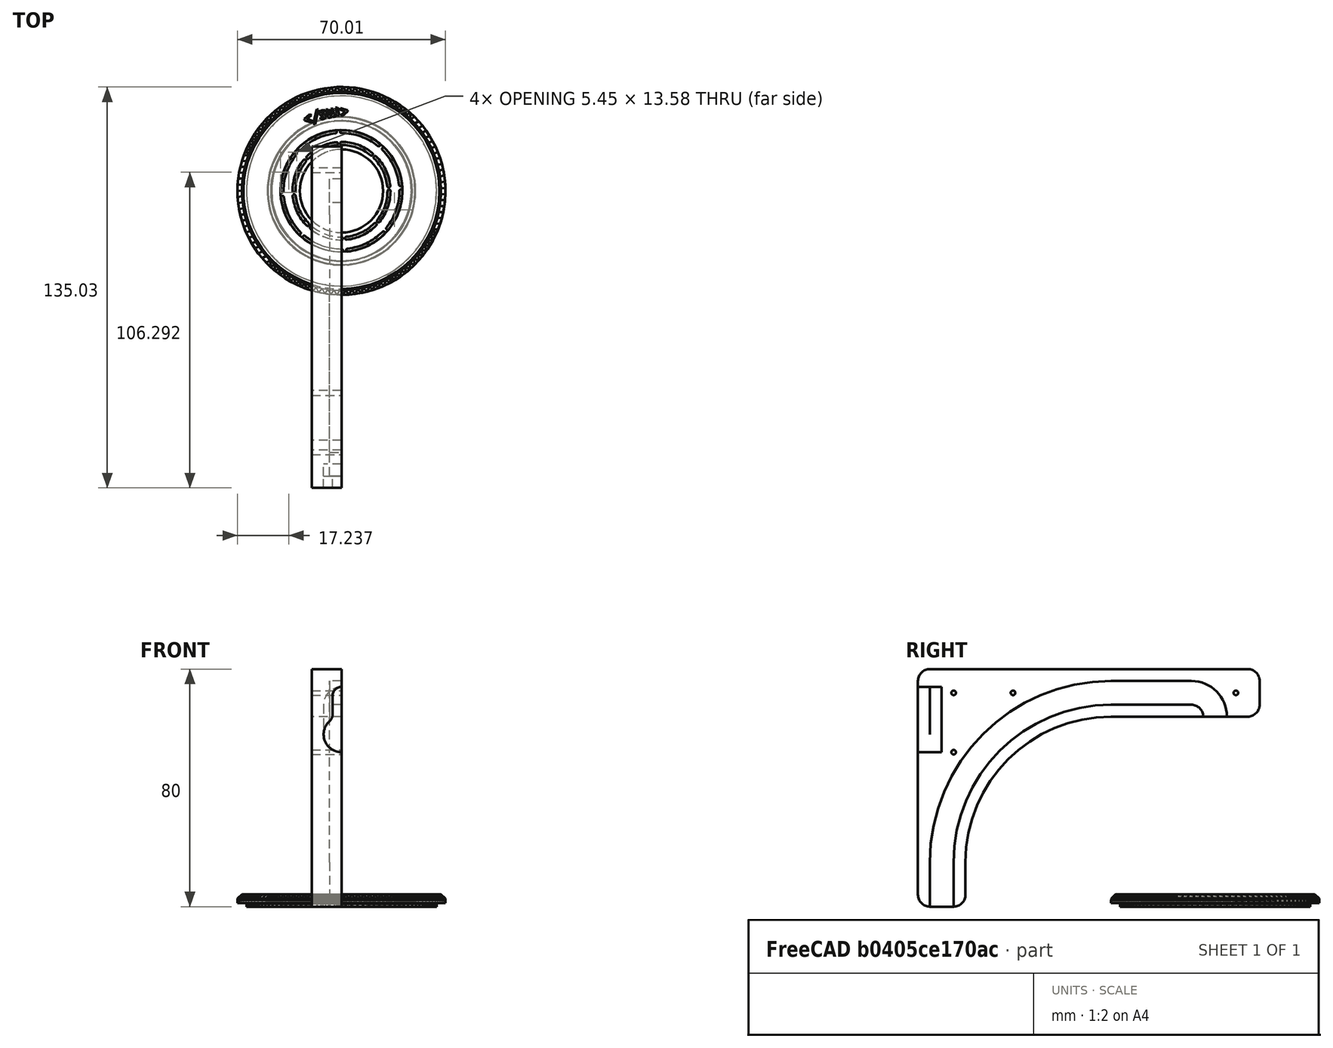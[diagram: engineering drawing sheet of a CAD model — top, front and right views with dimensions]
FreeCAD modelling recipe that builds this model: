
FCSTD DOCUMENT  (FreeCAD 1.0R39109 (Git))
Label: lampshade
License: All rights reserved
LicenseURL: http://www.ohwr.org/attachments/2388/cern_ohl_v_1_2.txt
objects: Sketcher::SketchObject×11, PartDesign::Pocket×6, PartDesign::Pad×5, Part::Feature×4, Mesh::Feature×3, PartDesign::SubShapeBinder×3, PartDesign::Body×3, PartDesign::PolarPattern×2, PartDesign::Chamfer×1, PartDesign::Fillet×1, Part::FeaturePython×1, Part::Mirroring×1
note: 77 computed .brp shape members not serialized (recipe doc carries the construction recipe); baked Part::Feature solids carry a one-line shape summary decoded from their .brp

FEATURE [Mesh::Feature] obj_1_Checkerboard_v6  label="obj_1_Checkerboard v6"
  Placement = pos=(89.8,-89.8,1.1) rot=(0,1,0;3.14159rad)
FEATURE [Mesh::Feature] obj_2_cordset_holder_bottom__E27_  label="obj_2_cordset holder bottom (E27)"
FEATURE [Mesh::Feature] obj_1_cordset_holder_top__E27_  label="obj_1_cordset holder top (E27)"
  Placement = pos=(-68.3,-1.4,0) rot=(0,0,1;0rad)
FEATURE [Part::Feature] obj_1_cordset_holder_top__E27_001
  shape: bbox 69.98 x 69.99 x 3 mm, 2374 faces, 0 solids (baked)
FEATURE [Part::Feature] obj_1_cordset_holder_top__E27_001_solid  label="obj_1_cordset_holder_top__E27_001 (Solid)"
  Placement = pos=(-75.6225,-88.5627,1.2) rot=(0,0,1;0rad)
  shape: bbox 69.98 x 69.99 x 3 mm, 2374 faces (baked)
FEATURE [Part::Feature] obj_2_cordset_holder_bottom__E27_001
  shape: bbox 63.99 x 63.99 x 2.5 mm, 1452 faces, 0 solids (baked)
FEATURE [Part::Feature] obj_2_cordset_holder_bottom__E27_001_solid  label="obj_2_cordset_holder_bottom__E27_001 (Solid)"
  Placement = pos=(-74.9737,-87.9749,0) rot=(0,0,1;0rad)
  shape: bbox 63.99 x 63.99 x 2.5 mm, 1452 faces (baked)
FEATURE [Sketcher::SketchObject] Sketch
  ArcFitTolerance = 1e-06
  AttachmentSupport = -> [XY_Plane]
  FullyConstrained = true
  MakeInternals = false
  MapMode = 5
  sketch-geometry (2):
    g0: Circle CenterX=0 CenterY=0 CenterZ=0 NormalX=0 NormalY=0 NormalZ=1 AngleXU=0 Radius=32
    g1: Circle CenterX=0 CenterY=0 CenterZ=0 NormalX=0 NormalY=0 NormalZ=1 AngleXU=0 Radius=14
  constraints (4):
    c: Coincident(g0,g-1)
    c: Coincident(g1,g0)
    c: Diameter(g1) = 28  'dia_inner'
    c: Diameter(g0) = 64  'dia_outer'
FEATURE [PartDesign::SubShapeBinder] Binder
  BindCopyOnChange = 0
  BindMode = 0
  ClaimChildren = false
  Context = -> Body [Binder.]
  Fuse = false
  MakeFace = true
  OffsetFill = false
  OffsetIntersection = false
  OffsetJoinType = 0
  OffsetOpenResult = false
  PartialLoad = false
  Refine = true
  Relative = true
  Support = -> [obj_2_cordset_holder_bottom__E27_001_solid]
  _Version = 2
FEATURE [PartDesign::Pad] Pad
  Direction = (0,0,1)
  Length = 1
  Length2 = 10
  Profile = -> Sketch
  ReferenceAxis = -> Sketch [N_Axis]
  Refine = true
  Suppressed = false
  Type = 0
FEATURE [Sketcher::SketchObject] Sketch001
  ArcFitTolerance = 1e-06
  AttachmentSupport = -> [Pad]
  FullyConstrained = true
  MakeInternals = false
  MapMode = 5
  Placement = pos=(0,0,1) rot=(0,0,1;0rad)
  sketch-geometry (2):
    g0: Circle CenterX=0 CenterY=0 CenterZ=0 NormalX=0 NormalY=0 NormalZ=1 AngleXU=0 Radius=23.75
    g1: Circle CenterX=0 CenterY=0 CenterZ=0 NormalX=0 NormalY=0 NormalZ=1 AngleXU=0 Radius=24.75
  constraints (4):
    c: Coincident(g0,g-1)
    c: Coincident(g1,g0)
    c: Diameter(g0) = 47.5  'lip_dia_inner'
    c: Diameter(g1) = 49.5  'lip_dia_outer'
FEATURE [PartDesign::Pad] Pad001
  BaseFeature = -> Pad
  Direction = (0,0,1)
  Length = 1.5
  Length2 = 10
  Profile = -> Sketch001
  ReferenceAxis = -> Sketch001 [N_Axis]
  Refine = true
  Suppressed = false
  Type = 0
FEATURE [Sketcher::SketchObject] Sketch002
  ArcFitTolerance = 1e-06
  AttachmentSupport = -> [Pad001]
  FullyConstrained = true
  MakeInternals = false
  MapMode = 5
  Placement = pos=(0,0,1) rot=(0,0,1;0rad)
  sketch-geometry (12):
    g0: ArcOfCircle CenterX=0 CenterY=0 CenterZ=0 NormalX=0 NormalY=0 NormalZ=1 AngleXU=0 Radius=15.5 StartAngle=0.890118 EndAngle=1.5708
    g1: ArcOfCircle CenterX=0 CenterY=0 CenterZ=0 NormalX=0 NormalY=0 NormalZ=1 AngleXU=0 Radius=16.5 StartAngle=0.890118 EndAngle=1.5708
    g2: ArcOfCircle CenterX=0 CenterY=0 CenterZ=0 NormalX=0 NormalY=0 NormalZ=1 AngleXU=0 Radius=19.5 StartAngle=0.890118 EndAngle=1.5708
    g3: ArcOfCircle CenterX=0 CenterY=0 CenterZ=0 NormalX=0 NormalY=0 NormalZ=1 AngleXU=0 Radius=20.5 StartAngle=0.890118 EndAngle=1.5708
    g4: ArcOfCircle CenterX=0 CenterY=16 CenterZ=0 NormalX=0 NormalY=0 NormalZ=1 AngleXU=0 Radius=0.5 StartAngle=1.5708 EndAngle=4.71239
    g5: ArcOfCircle CenterX=0 CenterY=20 CenterZ=0 NormalX=0 NormalY=0 NormalZ=1 AngleXU=0 Radius=0.5 StartAngle=1.5708 EndAngle=4.71239
    g6: ArcOfCircle CenterX=10.0691 CenterY=12.4343 CenterZ=0 NormalX=0 NormalY=0 NormalZ=1 AngleXU=0 Radius=0.5 StartAngle=4.03171 EndAngle=7.1733
    g7: ArcOfCircle CenterX=12.5864 CenterY=15.5429 CenterZ=0 NormalX=0 NormalY=0 NormalZ=1 AngleXU=0 Radius=0.5 StartAngle=4.03171 EndAngle=7.1733
    g8: LineSegment [constr] StartX=0 StartY=20 StartZ=0 EndX=0 EndY=16 EndZ=0
    g9: LineSegment [constr] StartX=12.2717 StartY=15.1543 StartZ=0 EndX=10.0691 EndY=12.4343 EndZ=0
    g10: LineSegment [constr] StartX=9.75447 StartY=12.0458 StartZ=0 EndX=0 EndY=0 EndZ=0
    g11: LineSegment [constr] StartX=0 StartY=16 StartZ=0 EndX=0 EndY=0 EndZ=0
  constraints (32):
    c: PointOnObject(g0,g-2)
    c: PointOnObject(g11,g-2)
    c: PointOnObject(g1,g-2)
    c: PointOnObject(g2,g-2)
    c: PointOnObject(g3,g-2)
    c: Coincident(g4,g1)
    c: Coincident(g4,g0)
    c: PointOnObject(g5,g-2)
    c: Coincident(g5,g3)
    c: Coincident(g5,g2)
    c: Tangent(g6,g0) = 1.5708
    c: Tangent(g6,g1) = -1.5708
    c: Tangent(g7,g2) = 1.5708
    c: Tangent(g7,g3) = -1.5708
    c: Equal(g5,g4)
    c: Radius(g4) = 0.5
    c: DistanceY(g0,g5) = 20
    c: Coincident(g8,g5)
    c: Coincident(g8,g4)
    c: Coincident(g9,g2)
    c: Coincident(g9,g6)
    c: Coincident(g10,g0)
    c: Parallel(g10,g9)
    c: Angle(g10,g11) = 0.680678
    c: DistanceY(g-1,g4) = 16
    c: Coincident(g0,g1)
    c: Coincident(g0,g2)
    c: Coincident(g0,g3)
    c: Coincident(g0,g10)
    c: Coincident(g0,g11)
    c: Coincident(g0,g-1)
    c: Coincident(g11,g4)
FEATURE [PartDesign::Pocket] Pocket
  BaseFeature = -> Pad001
  Direction = (0,0,-1)
  Length = 5
  Length2 = 5
  Profile = -> Sketch002
  ReferenceAxis = -> Sketch002 [N_Axis]
  Refine = true
  Suppressed = false
  Type = 1
FEATURE [PartDesign::PolarPattern] PolarPattern
  Angle = 360
  Axis = -> Sketch002 [N_Axis]
  BaseFeature = -> Pocket
  Mode = 0
  Occurrences = 8
  Offset = 120
  Originals = -> [Pocket]
  Refine = true
  Suppressed = false
  TransformMode = 0
FEATURE [PartDesign::Body] Body  label="Ring_upper"
  AllowCompound = false
  Group = -> [Sketch,Binder,Pad,Sketch001,Pad001,Sketch002,Pocket,PolarPattern]
  Origin = -> Origin
  Tip = -> PolarPattern
FEATURE [PartDesign::SubShapeBinder] Binder001
  BindCopyOnChange = 0
  BindMode = 0
  ClaimChildren = false
  Context = -> Body001 [Binder001.]
  Fuse = false
  MakeFace = true
  OffsetFill = false
  OffsetIntersection = false
  OffsetJoinType = 0
  OffsetOpenResult = false
  PartialLoad = false
  Refine = true
  Relative = true
  Support = -> [obj_1_cordset_holder_top__E27_001_solid]
  _Version = 2
FEATURE [Sketcher::SketchObject] Sketch003
  ArcFitTolerance = 1e-06
  AttachmentSupport = -> [XY_Plane001]
  FullyConstrained = true
  MakeInternals = false
  MapMode = 5
  expr: Constraints[2] = Sketch.Constraints.dia_inner
  expr: Constraints[3] = Sketch.Constraints.dia_outer + 6 mm
  sketch-geometry (2):
    g0: Circle CenterX=0 CenterY=0 CenterZ=0 NormalX=0 NormalY=0 NormalZ=1 AngleXU=0 Radius=14
    g1: Circle CenterX=0 CenterY=0 CenterZ=0 NormalX=0 NormalY=0 NormalZ=1 AngleXU=0 Radius=35
  constraints (4):
    c: Coincident(g0,g-1)
    c: Coincident(g1,g0)
    c: Diameter(g0) = 28
    c: Diameter(g1) = 70
FEATURE [PartDesign::Pad] Pad002
  Direction = (0,0,1)
  Length = 3
  Length2 = 10
  Profile = -> Sketch003
  ReferenceAxis = -> Sketch003 [N_Axis]
  Refine = true
  Suppressed = false
  Type = 0
FEATURE [Sketcher::SketchObject] Sketch004
  ArcFitTolerance = 1e-06
  AttachmentSupport = -> [Pad002]
  FullyConstrained = true
  MakeInternals = false
  MapMode = 5
  Placement = pos=(0,0,0) rot=(1,0,0;3.14159rad)
  expr: Constraints[2] = Sketch001.Constraints.lip_dia_inner - 0.5 mm
  expr: Constraints[3] = Sketch001.Constraints.lip_dia_outer + 0.5 mm
  sketch-geometry (2):
    g0: Circle CenterX=0 CenterY=0 CenterZ=0 NormalX=0 NormalY=0 NormalZ=1 AngleXU=0 Radius=23.5
    g1: Circle CenterX=0 CenterY=0 CenterZ=0 NormalX=0 NormalY=0 NormalZ=1 AngleXU=0 Radius=25
  constraints (4):
    c: Coincident(g0,g-1)
    c: Coincident(g1,g0)
    c: Diameter(g0) = 47
    c: Diameter(g1) = 50
FEATURE [PartDesign::Pocket] Pocket001
  BaseFeature = -> Pad002
  Direction = (0,0,1)
  Length = 1.7
  Length2 = 5
  Profile = -> Sketch004
  ReferenceAxis = -> Sketch004 [N_Axis]
  Refine = true
  Suppressed = false
  Type = 0
FEATURE [PartDesign::SubShapeBinder] Binder002
  BindCopyOnChange = 0
  BindMode = 0
  ClaimChildren = false
  Context = -> Body001 [Binder002.]
  Fuse = false
  MakeFace = true
  OffsetFill = false
  OffsetIntersection = false
  OffsetJoinType = 0
  OffsetOpenResult = false
  PartialLoad = false
  Refine = true
  Relative = true
  Support = -> [Body]
  _Version = 2
FEATURE [Sketcher::SketchObject] Sketch005
  ArcFitTolerance = 1e-06
  AttachmentSupport = -> [Pocket001]
  ExternalGeometry = -> [Binder002]
  FullyConstrained = true
  MakeInternals = false
  MapMode = 5
  Placement = pos=(0,0,0) rot=(1,0,0;3.14159rad)
  sketch-geometry (8):
    g0: ArcOfCircle CenterX=1.4e-15 CenterY=1e-16 CenterZ=0 NormalX=0 NormalY=0 NormalZ=1 AngleXU=0 Radius=15.5 StartAngle=0.785398 EndAngle=1.46608
    g1: ArcOfCircle CenterX=1.2e-15 CenterY=8e-16 CenterZ=0 NormalX=0 NormalY=0 NormalZ=1 AngleXU=0 Radius=16.5 StartAngle=0.785398 EndAngle=1.46608
    g2: ArcOfCircle CenterX=-2.6e-15 CenterY=4e-15 CenterZ=0 NormalX=0 NormalY=0 NormalZ=1 AngleXU=0 Radius=19.5 StartAngle=0.785398 EndAngle=1.46608
    g3: ArcOfCircle CenterX=-2.5e-15 CenterY=4.2e-15 CenterZ=0 NormalX=0 NormalY=0 NormalZ=1 AngleXU=0 Radius=20.5 StartAngle=0.785398 EndAngle=1.46608
    g4: ArcOfCircle CenterX=2.09057 CenterY=19.8904 CenterZ=0 NormalX=0 NormalY=0 NormalZ=1 AngleXU=0 Radius=0.5 StartAngle=1.46608 EndAngle=4.60767
    g5: ArcOfCircle CenterX=14.1421 CenterY=14.1421 CenterZ=0 NormalX=0 NormalY=0 NormalZ=1 AngleXU=0 Radius=0.5 StartAngle=3.92699 EndAngle=7.06858
    g6: ArcOfCircle CenterX=11.3137 CenterY=11.3137 CenterZ=0 NormalX=0 NormalY=0 NormalZ=1 AngleXU=0 Radius=0.5 StartAngle=3.92699 EndAngle=7.06858
    g7: ArcOfCircle CenterX=1.67246 CenterY=15.9124 CenterZ=0 NormalX=0 NormalY=0 NormalZ=1 AngleXU=0 Radius=0.5 StartAngle=1.46608 EndAngle=4.60767
  constraints (20):
    c: Coincident(g0,g-6)
    c: Coincident(g0,g-6)
    c: Equal(g-6,g0)
    c: Coincident(g1,g-5)
    c: Coincident(g1,g-5)
    c: Equal(g1,g-5)
    c: Coincident(g2,g-4)
    c: Coincident(g2,g-4)
    c: Equal(g2,g-4)
    c: Coincident(g3,g-3)
    c: Coincident(g3,g-3)
    c: Equal(g3,g-3)
    c: Coincident(g4,g2)
    c: Tangent(g4,g3) = -1.5708
    c: Coincident(g5,g2)
    c: Tangent(g5,g3) = -1.5708
    c: Coincident(g6,g0)
    c: Tangent(g6,g1) = -1.5708
    c: Coincident(g7,g0)
    c: Tangent(g7,g1) = -1.5708
FEATURE [PartDesign::Pocket] Pocket002
  BaseFeature = -> Pocket001
  Direction = (0,0,1)
  Length = 5
  Length2 = 5
  Profile = -> Sketch005
  ReferenceAxis = -> Sketch005 [N_Axis]
  Refine = true
  Suppressed = false
  Type = 1
FEATURE [PartDesign::PolarPattern] PolarPattern001
  Angle = 360
  Axis = -> Sketch005 [N_Axis]
  BaseFeature = -> Pocket002
  Mode = 0
  Occurrences = 8
  Offset = 120
  Originals = -> [Pocket002]
  Refine = true
  Suppressed = false
  TransformMode = 0
FEATURE [PartDesign::Chamfer] Chamfer
  Angle = 45
  Base = -> PolarPattern001 [Edge3]
  BaseFeature = -> PolarPattern001
  ChamferType = 0
  FlipDirection = false
  Refine = true
  Size = 2
  Size2 = 1
  SupportTransform = false
  Suppressed = false
  UseAllEdges = false
FEATURE [PartDesign::Body] Body001  label="Ring_lower"
  AllowCompound = false
  Group = -> [Binder001,Sketch003,Pad002,Sketch004,Pocket001,Binder002,Sketch005,Pocket002,PolarPattern001,Chamfer]
  Origin = -> Origin001
  Placement = pos=(0,0,1.2) rot=(0,0,1;0rad)
  Tip = -> Chamfer
FEATURE [Sketcher::SketchObject] Sketch006
  ArcFitTolerance = 1e-06
  AttachmentSupport = -> [YZ_Plane002]
  FullyConstrained = true
  MakeInternals = false
  MapMode = 5
  Placement = pos=(0,0,0) rot=(0.57735,0.57735,0.57735;2.0944rad)
  sketch-geometry (7):
    g0: LineSegment StartX=-100 StartY=80 StartZ=0 EndX=15 EndY=80 EndZ=0
    g1: LineSegment StartX=15 StartY=80 StartZ=0 EndX=15 EndY=64 EndZ=0
    g2: LineSegment StartX=15 StartY=64 StartZ=0 EndX=-35 EndY=64 EndZ=0
    g3: ArcOfCircle CenterX=-35 CenterY=15 CenterZ=0 NormalX=0 NormalY=0 NormalZ=1 AngleXU=0 Radius=49 StartAngle=1.5708 EndAngle=3.14159
    g4: LineSegment StartX=-84 StartY=15 StartZ=0 EndX=-84 EndY=1.8e-15 EndZ=0
    g5: LineSegment StartX=-84 StartY=1.8e-15 StartZ=0 EndX=-100 EndY=0 EndZ=0
    g6: LineSegment StartX=-100 StartY=0 StartZ=0 EndX=-100 EndY=80 EndZ=0
  constraints (19):
    c: Horizontal(g0)
    c: Coincident(g0,g1)
    c: Vertical(g1)
    c: Coincident(g1,g2)
    c: Horizontal(g2)
    c: Tangent(g2,g3) = -1.5708
    c: Tangent(g3,g4) = -1.5708
    c: Coincident(g4,g5)
    c: Coincident(g5,g6)
    c: Coincident(g6,g0)
    c: Vertical(g6)
    c: Vertical(g4)
    c: Equal(g5,g1)
    c: DistanceY(g1,g1) = 16
    c: DistanceX(g0,g0) = 115
    c: Distance(g0,g-2) = 15
    c: DistanceX(g2,g2) = 50
    c: Distance(g4,g4) = 15
    c: Tangent(g5,g-1) = 1.5708
FEATURE [PartDesign::Pad] Pad003
  Direction = (1,0,0)
  Length = 10
  Length2 = 10
  Placement = pos=(0,0,0) rot=(1,1,1;2.0944rad)
  Profile = -> Sketch006
  ReferenceAxis = -> Sketch006 [N_Axis]
  Refine = true
  Suppressed = false
  Type = 0
FEATURE [Sketcher::SketchObject] Sketch007
  ArcFitTolerance = 1e-06
  AttachmentSupport = -> [Pad003]
  ExternalGeometry = -> [Pad003]
  FullyConstrained = true
  MakeInternals = false
  MapMode = 5
  Placement = pos=(3e-16,0,0) rot=(0.57735,0.57735,-0.57735;4.18879rad)
  sketch-geometry (10):
    g0: LineSegment StartX=-88 StartY=-3.06e-14 StartZ=0 EndX=-88 EndY=-15 EndZ=0
    g1: ArcOfCircle CenterX=-35 CenterY=-15 CenterZ=0 NormalX=0 NormalY=0 NormalZ=1 AngleXU=0 Radius=53 StartAngle=3.14159 EndAngle=4.71239
    g2: LineSegment StartX=-35 StartY=-68 StartZ=0 EndX=-8 EndY=-68 EndZ=0
    g3: ArcOfCircle CenterX=-8 CenterY=-64 CenterZ=0 NormalX=0 NormalY=0 NormalZ=1 AngleXU=0 Radius=4 StartAngle=4.71239 EndAngle=6.28319
    g4: LineSegment StartX=-4 StartY=-64 StartZ=0 EndX=4 EndY=-64 EndZ=0
    g5: ArcOfCircle CenterX=-8 CenterY=-64 CenterZ=0 NormalX=0 NormalY=0 NormalZ=1 AngleXU=0 Radius=12 StartAngle=4.71239 EndAngle=6.28319
    g6: LineSegment StartX=-8 StartY=-76 StartZ=0 EndX=-35 EndY=-76 EndZ=0
    g7: ArcOfCircle CenterX=-35 CenterY=-15 CenterZ=0 NormalX=0 NormalY=0 NormalZ=1 AngleXU=0 Radius=61 StartAngle=3.14159 EndAngle=4.71239
    g8: LineSegment StartX=-96 StartY=-15 StartZ=0 EndX=-96 EndY=-3.2e-14 EndZ=0
    g9: LineSegment StartX=-96 StartY=-3.2e-14 StartZ=0 EndX=-88 EndY=-3.06e-14 EndZ=0
  constraints (23):
    c: PointOnObject(g0,g-6)
    c: Vertical(g0)
    c: Tangent(g0,g1) = -1.5708
    c: Tangent(g1,g2) = -1.5708
    c: Tangent(g2,g3) = -1.5708
    c: PointOnObject(g3,g-5)
    c: Coincident(g3,g4)
    c: Perpendicular(g4,g5) = 1.5708
    c: Horizontal(g6)
    c: Tangent(g6,g7) = 1.5708
    c: PointOnObject(g8,g-6)
    c: Vertical(g8)
    c: Coincident(g8,g9)
    c: Coincident(g9,g0)
    c: Coincident(g1,g7)
    c: Coincident(g1,g-4)
    c: Coincident(g3,g5)
    c: Tangent(g5,g6) = 1.5708
    c: Tangent(g7,g8) = 1.5708
    c: Symmetric(g3,g4,g-2)
    c: Distance(g4,g4) = 8
    c: Radius(g3) = 4
    c: Horizontal(g2)
FEATURE [PartDesign::Pocket] Pocket003
  BaseFeature = -> Pad003
  Direction = (1,0,0)
  Length = 4
  Length2 = 5
  Placement = pos=(0,0,0) rot=(1,1,1;2.0944rad)
  Profile = -> Sketch007
  ReferenceAxis = -> Sketch007 [N_Axis]
  Refine = true
  Suppressed = false
  Type = 0
FEATURE [Sketcher::SketchObject] Sketch008
  ArcFitTolerance = 1e-06
  AttachmentSupport = -> [Pocket003]
  ExternalGeometry = -> [Pocket003]
  FullyConstrained = true
  MakeInternals = false
  MapMode = 5
  Placement = pos=(6e-16,0,0) rot=(0.57735,0.57735,-0.57735;4.18879rad)
  sketch-geometry (10):
    g0: Circle CenterX=-88 CenterY=-52 CenterZ=0 NormalX=0 NormalY=0 NormalZ=1 AngleXU=0 Radius=0.775
    g1: Circle CenterX=-68 CenterY=-72 CenterZ=0 NormalX=0 NormalY=0 NormalZ=1 AngleXU=0 Radius=0.775
    g2: Circle CenterX=-88 CenterY=-72 CenterZ=0 NormalX=0 NormalY=0 NormalZ=1 AngleXU=0 Radius=0.775
    g3: Circle CenterX=7 CenterY=-72 CenterZ=0 NormalX=0 NormalY=0 NormalZ=1 AngleXU=0 Radius=0.775
    g4: LineSegment [constr] StartX=-88 StartY=-52 StartZ=0 EndX=-88 EndY=-72 EndZ=0
    g5: LineSegment [constr] StartX=-88 StartY=-72 StartZ=0 EndX=-68 EndY=-72 EndZ=0
    g6: LineSegment [constr] StartX=-68 StartY=-72 StartZ=0 EndX=7 EndY=-72 EndZ=0
    g7: LineSegment [constr] StartX=7 StartY=-72 StartZ=0 EndX=15 EndY=-72 EndZ=0
    g8: LineSegment [constr] StartX=-88 StartY=-72 StartZ=0 EndX=-100 EndY=-72 EndZ=0
    g9: LineSegment [constr] StartX=-88 StartY=-72 StartZ=0 EndX=-88 EndY=-80 EndZ=0
  constraints (26):
    c: Coincident(g4,g0)
    c: Coincident(g4,g2)
    c: Vertical(g4)
    c: Coincident(g5,g2)
    c: Coincident(g5,g1)
    c: Coincident(g6,g1)
    c: Coincident(g6,g3)
    c: Horizontal(g6)
    c: Coincident(g7,g3)
    c: Horizontal(g7)
    c: Horizontal(g5)
    c: Symmetric(g-3,g-4,g7)
    c: Equal(g0,g2)
    c: Equal(g2,g1)
    c: Equal(g1,g3)
    c: Diameter(g0) = 1.55
    c: Equal(g4,g5)
    c: Coincident(g8,g2)
    c: PointOnObject(g8,g-5)
    c: Horizontal(g8)
    c: Coincident(g9,g2)
    c: PointOnObject(g9,g-4)
    c: Vertical(g9)
    c: DistanceY(g4,g4) = 20
    c: DistanceX(g7,g7) = 8
    c: DistanceX(g8,g8) = 12
FEATURE [PartDesign::Pocket] Pocket004
  BaseFeature = -> Pocket003
  Direction = (1,0,0)
  Length = 5
  Length2 = 5
  Placement = pos=(0,0,0) rot=(1,1,1;2.0944rad)
  Profile = -> Sketch008
  ReferenceAxis = -> Sketch008 [N_Axis]
  Refine = true
  Suppressed = false
  Type = 1
FEATURE [PartDesign::Fillet] Fillet
  Base = -> Pocket004 [Edge8,Edge2,Edge1,Edge5,Edge33]
  BaseFeature = -> Pocket004
  Placement = pos=(0,0,0) rot=(1,1,1;2.0944rad)
  Radius = 4
  Refine = true
  SupportTransform = false
  Suppressed = false
  UseAllEdges = false
FEATURE [Sketcher::SketchObject] Sketch009
  ArcFitTolerance = 1e-06
  AttachmentSupport = -> [Fillet]
  ExternalGeometry = -> [Fillet]
  FullyConstrained = true
  MakeInternals = false
  MapMode = 5
  Placement = pos=(-2.22e-14,-100,7.77e-14) rot=(0.57735,0.57735,-0.57735;2.0944rad)
  sketch-geometry (4):
    g0: ArcOfCircle CenterX=-68 CenterY=0 CenterZ=0 NormalX=0 NormalY=0 NormalZ=1 AngleXU=0 Radius=6 StartAngle=1.5708 EndAngle=4.71239
    g1: ArcOfCircle CenterX=-58 CenterY=-1e-16 CenterZ=0 NormalX=0 NormalY=0 NormalZ=1 AngleXU=0 Radius=6 StartAngle=4.71239 EndAngle=7.85398
    g2: LineSegment StartX=-68 StartY=6 StartZ=0 EndX=-58 EndY=6 EndZ=0
    g3: LineSegment StartX=-68 StartY=-6 StartZ=0 EndX=-58 EndY=-6 EndZ=0
  constraints (10):
    c: Tangent(g0,g2) = 1.5708
    c: Tangent(g0,g3) = -1.5708
    c: Tangent(g1,g2) = 1.5708
    c: Tangent(g1,g3) = -1.5708
    c: Equal(g0,g1)
    c: Horizontal(g3)
    c: PointOnObject(g0,g-1)
    c: Radius(g1) = 6
    c: DistanceX(g2,g2) = 10
    c: DistanceX(g-3,g0) = 12
FEATURE [PartDesign::Pocket] Pocket005
  BaseFeature = -> Fillet
  Direction = (0,1,0)
  Length = 8
  Length2 = 5
  Placement = pos=(0,0,0) rot=(1,1,1;2.0944rad)
  Profile = -> Sketch009
  ReferenceAxis = -> Sketch009 [N_Axis]
  Refine = true
  Suppressed = false
  Type = 0
FEATURE [Sketcher::SketchObject] Sketch010
  ArcFitTolerance = 1e-06
  AttachmentSupport = -> [Pocket005]
  ExternalGeometry = -> [Pocket005]
  FullyConstrained = true
  MakeInternals = false
  MapMode = 5
  Placement = pos=(-2.22e-14,-100,1.11e-13) rot=(0.57735,0.57735,-0.57735;2.0944rad)
  sketch-geometry (6):
    g0: ArcOfCircle CenterX=-71 CenterY=0 CenterZ=0 NormalX=0 NormalY=0 NormalZ=1 AngleXU=0 Radius=3 StartAngle=1.5708 EndAngle=3.14159
    g1: LineSegment StartX=-71 StartY=3 StartZ=0 EndX=-64.7082 EndY=3 EndZ=0
    g2: ArcOfCircle CenterX=-64.7082 CenterY=6 CenterZ=0 NormalX=0 NormalY=0 NormalZ=1 AngleXU=0 Radius=3 StartAngle=4.71239 EndAngle=5.55346
    g3: ArcOfCircle CenterX=-58 CenterY=-3.23e-14 CenterZ=0 NormalX=0 NormalY=0 NormalZ=1 AngleXU=0 Radius=6 StartAngle=1.5708 EndAngle=2.41186
    g4: LineSegment StartX=-58 StartY=6 StartZ=0 EndX=-68 EndY=6 EndZ=0
    g5: ArcOfCircle CenterX=-68 CenterY=-3.77e-14 CenterZ=0 NormalX=0 NormalY=0 NormalZ=1 AngleXU=0 Radius=6 StartAngle=1.5708 EndAngle=3.14159
  constraints (14):
    c: PointOnObject(g5,g-1)
    c: Coincident(g5,g0) = 1.5708
    c: Horizontal(g1)
    c: Tangent(g4,g5) = -1.5708
    c: Tangent(g0,g1) = 1.5708
    c: Coincident(g5,g-3)
    c: Tangent(g3,g4) = -1.5708
    c: PointOnObject(g0,g-1)
    c: Radius(g0) = 3
    c: Coincident(g3,g-4)
    c: Coincident(g3,g-4)
    c: Tangent(g2,g3) = 1.5708
    c: Tangent(g1,g2) = -1.5708
    c: PointOnObject(g2,g4)
FEATURE [PartDesign::Pad] Pad004
  BaseFeature = -> Pocket005
  Direction = (-1e-16,-1,1e-15)
  Length = 4
  Length2 = 10
  Placement = pos=(0,0,0) rot=(1,1,1;2.0944rad)
  Profile = -> Sketch010
  ReferenceAxis = -> Sketch010 [N_Axis]
  Reversed = true
  Suppressed = false
  Type = 0
FEATURE [PartDesign::Body] Body002  label="Wall_mount_left"
  AllowCompound = false
  Group = -> [Sketch006,Pad003,Sketch007,Pocket003,Sketch008,Pocket004,Fillet,Sketch009,Pocket005,Sketch010,Pad004]
  Origin = -> Origin002
  Tip = -> Pad004
FEATURE [Part::FeaturePython] Clone  label="Wall_mount_left001"  # Draft clone (typed FeaturePython)
  AttacherType = Attacher::AttachEngine3D
  Fuse = false
  Objects = -> [Body002]
  Scale = (1,1,1)
FEATURE [Part::Mirroring] Mirror  label="Wall_mount_right (mirrored)"
  Base = (0,0,0)
  Normal = (-1,0,0)
  Source = -> Clone
